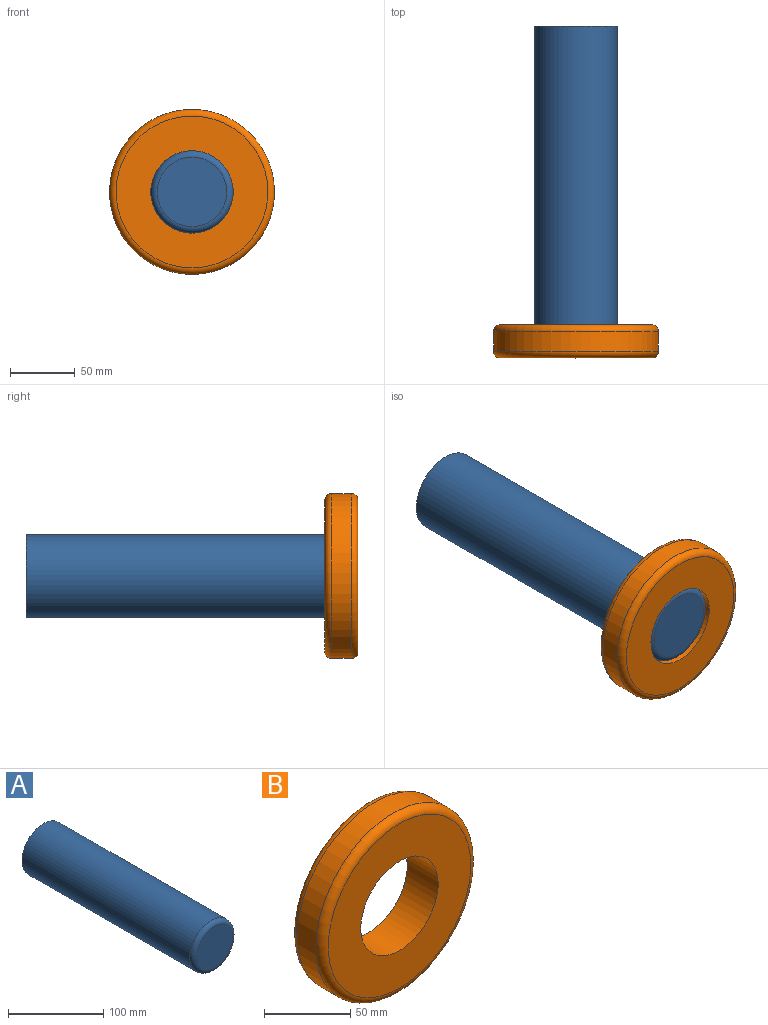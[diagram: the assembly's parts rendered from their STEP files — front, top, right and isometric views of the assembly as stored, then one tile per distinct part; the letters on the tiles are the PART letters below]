
ASSEMBLY  parts=2 mates=1
PART A: 4 faces, bbox 68.7x254x68.7 mm
  f0: cylinder r=31.75mm len=248.92mm, axis (0,1,0), area 49657.3mm2, adj f2,f3
  f1: plane 53.34x53.34mm, normal (0,-1,0), area 2234.6mm2, adj f3
  f2: plane 63.5x63.5mm, normal (0,1,0), area 3166.9mm2, adj f0
  f3: torus R=26.67mm, axis (0,-1,0), area 1499.3mm2, adj f0,f1
PART B: 6 faces, bbox 137.5x25.4x137.5 mm
  f0: cylinder r=63.5mm len=127mm, axis (0,1,0), area 6080.5mm2, adj f3,f4
  f1: plane 116.84x116.84mm, normal (0,-1,0), area 7555mm2, adj f3,f5
  f2: plane 116.84x116.84mm, normal (0,1,0), area 7555mm2, adj f4,f5
  f3: torus R=58.42mm, axis (0,-1,0), area 3091.2mm2, adj f0,f1
  f4: torus R=58.42mm, axis (0,-1,0), area 3091.2mm2, adj f0,f2
  f5: cylinder r=31.75mm len=63.5mm, axis (0,-1,0), area 5067.1mm2, adj f1,f2
PLACE A t=(-214.22,-13.99,268.5)mm
PLACE B t=(-214.22,-243.98,268.5)mm
MATE slider A.f0 <-> B.f5  axis (0,1,0) through (-214.22,-138.45,268.5)mm
